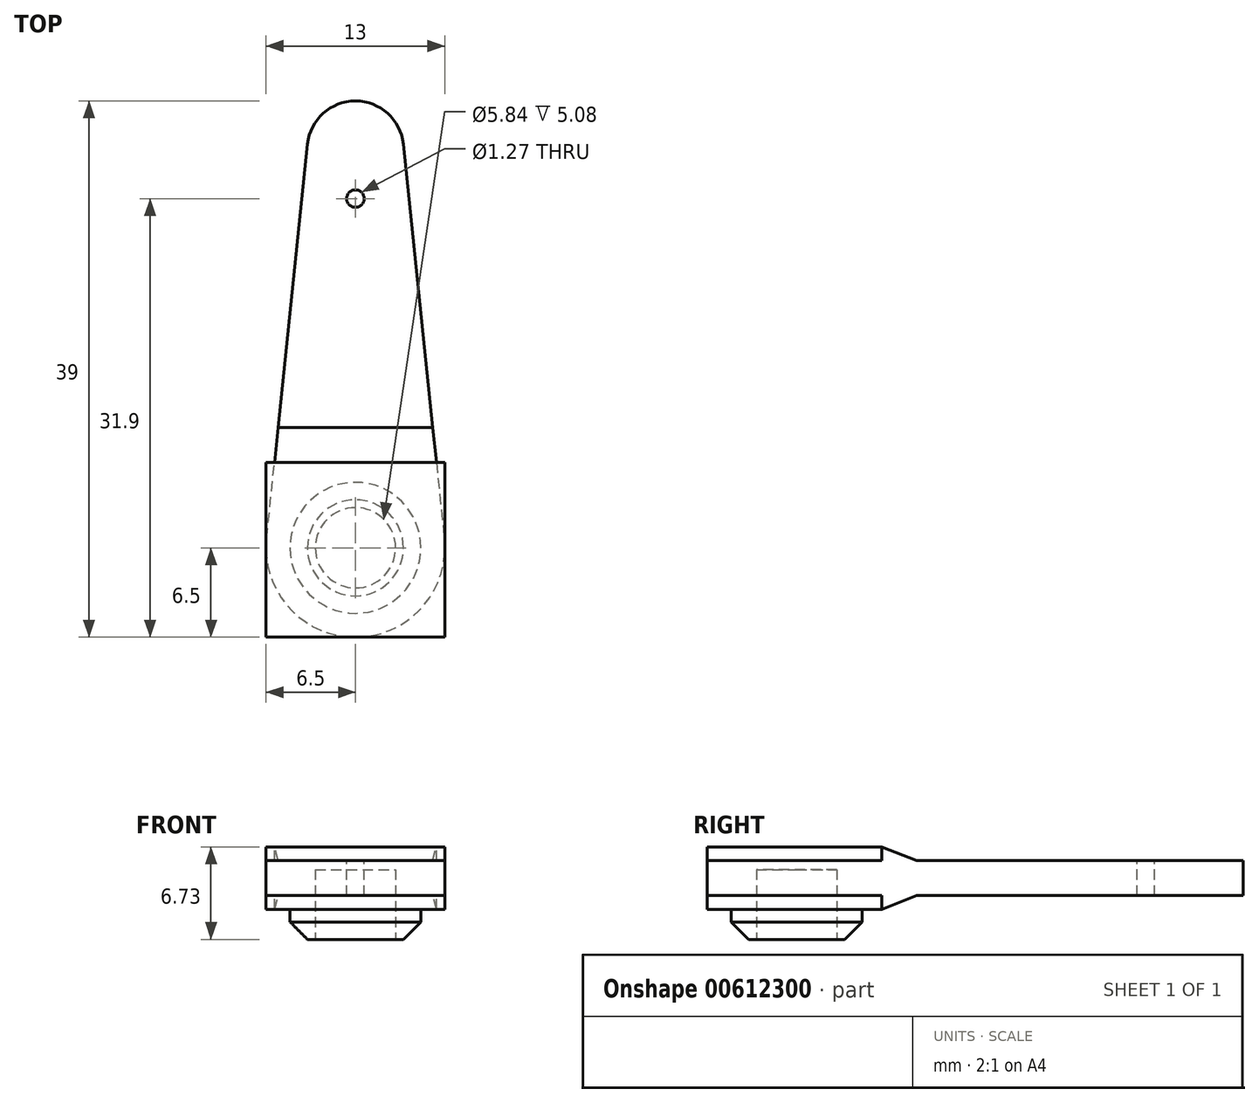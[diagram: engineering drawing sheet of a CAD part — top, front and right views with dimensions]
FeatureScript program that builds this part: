
annotation { "Feature Type Name" : "Feature", "Feature Type Description" : "" }
export const myFeature = defineFeature(function(context is Context, id is Id, definition is map)
    precondition{}
    {
        {
            var Q0;
            Q0=qCreatedBy(makeId("Top.planeOp"),FACE);
            var sketch = newSketch(context, id + "F0", { "sketchPlane" : qUnion([Q0])});
            skCircle(sketch, "E0", {"center": v(0, 0) * mm, "radius": 6.5 * mm});
            skCircle(sketch, "E1", {"center": v(0, 29) * mm, "radius": 3.5 * mm});
            skLineSegment(sketch, "E2", {"start": v(-6.47, 0.67) * mm, "end": v(-3.48, 29.36) * mm});
            skLineSegment(sketch, "E3", {"start": v(3.48, 29.36) * mm, "end": v(6.47, 0.67) * mm});
            skSolve(sketch);
        }
        {
            var Q0;
            Q0 = qSketchRegion(id + "F0", true);
            extrude(context, id + "F1", {"entities" : qUnion([Q0]), "endBound" : BoundingType.SYMMETRIC, "depth" : 2.54 * mm, "offsetDistance" : 25.4 * mm});
        }
        {
            var Q0;
            Q0=qCreatedBy(makeId("Right.planeOp"),FACE);
            var sketch = newSketch(context, id + "F2", { "sketchPlane" : qUnion([Q0])});
            skLineSegment(sketch, "E4.bottom", {"start": v(-6.5, 2.27) * mm, "end": v(6.2, 2.27) * mm});
            skLineSegment(sketch, "E4.top", {"start": v(-6.5, -2.27) * mm, "end": v(6.2, -2.27) * mm});
            skLineSegment(sketch, "E4.left", {"start": v(-6.5, 2.27) * mm, "end": v(-6.5, -2.27) * mm});
            skLineSegment(sketch, "E4.right", {"start": v(6.2, 2.27) * mm, "end": v(6.2, -2.27) * mm});
            skPoint(sketch, "E4.middle", {"position": v(-0.15, 0) * mm});
            skLineSegment(sketch, "E5.bottom", {"start": v(6.2, 1.27) * mm, "end": v(8.74, 1.27) * mm});
            skLineSegment(sketch, "E5.top", {"start": v(6.2, -1.27) * mm, "end": v(8.74, -1.27) * mm});
            skLineSegment(sketch, "E5.left", {"start": v(6.2, 1.27) * mm, "end": v(6.2, -1.27) * mm});
            skLineSegment(sketch, "E5.right", {"start": v(8.74, 1.27) * mm, "end": v(8.74, -1.27) * mm});
            skPoint(sketch, "E5.middle", {"position": v(7.47, 0) * mm});
            skLineSegment(sketch, "E6", {"start": v(6.2, 2.27) * mm, "end": v(8.74, 1.27) * mm});
            skLineSegment(sketch, "E7", {"start": v(8.74, -1.27) * mm, "end": v(6.2, -2.27) * mm});
            skLineSegment(sketch, "E8.bottom", {"start": v(6.2, 1.27) * mm, "end": v(-6.5, 1.27) * mm});
            skLineSegment(sketch, "E8.top", {"start": v(6.2, -1.27) * mm, "end": v(-6.5, -1.27) * mm});
            skLineSegment(sketch, "E8.right", {"start": v(-6.5, 1.27) * mm, "end": v(-6.5, -1.27) * mm});
            skSolve(sketch);
        }
        {
            var Q0;
            {var subQ0=sQuery(id+"F2.wireOp",EDGE,"E4.top");Q0=makeQuery(id+"F2.imprint","IMPRINT",FACE,{"disambiguationData":[TD([[makeQuery(id+"F2.imprint","IMPRINT",EDGE,{"derivedFrom":subQ0}),1.0]])]});}
            var Q1;
            {var subQ0=sQuery(id+"F2.wireOp",EDGE,"E4.bottom");Q1=makeQuery(id+"F2.imprint","IMPRINT",FACE,{"disambiguationData":[TD([[makeQuery(id+"F2.imprint","IMPRINT",EDGE,{"derivedFrom":subQ0}),-1.0]])]});}
            var Q2;
            {var subQ0=sQuery(id+"F2.wireOp",EDGE,"E6");Q2=makeQuery(id+"F2.imprint","IMPRINT",FACE,{"disambiguationData":[TD([[makeQuery(id+"F2.imprint","IMPRINT",EDGE,{"derivedFrom":subQ0}),-1.0]])]});}
            var Q3;
            {var subQ0=sQuery(id+"F2.wireOp",EDGE,"E7");Q3=makeQuery(id+"F2.imprint","IMPRINT",FACE,{"disambiguationData":[TD([[makeQuery(id+"F2.imprint","IMPRINT",EDGE,{"derivedFrom":subQ0}),-1.0]])]});}
            extrude(context, id + "F3", {"entities" : qUnion([Q0, Q1, Q2, Q3]), "operationType" : NewBodyOperationType.ADD, "endBound" : BoundingType.SYMMETRIC, "depth" : 13 * mm, "offsetDistance" : 25.4 * mm});
        }
        {
            var Q0;
            Q0=makeQuery(id+"F3.opExtrude","SWEPT_FACE",FACE,{"disambiguationData":[OSD([sQuery(id+"F2.wireOp",EDGE,"E4.bottom")])]});
            var sketch = newSketch(context, id + "F4", { "sketchPlane" : qUnion([Q0])});
            skArc(sketch, "E9.0.0", {"start": v(-6.47, 0.67) * mm, "mid": v(-6.5, 0.34) * mm, "end": v(-6.5, 0) * mm});
            skArc(sketch, "E9.0.1", {"start": v(-6.5, 0) * mm, "mid": v(-4.6, -4.6) * mm, "end": v(0, -6.5) * mm});
            skArc(sketch, "E9.0.2", {"start": v(0, -6.5) * mm, "mid": v(4.6, -4.6) * mm, "end": v(6.5, 0) * mm});
            skArc(sketch, "E9.0.3", {"start": v(6.5, 0) * mm, "mid": v(6.5, 0.34) * mm, "end": v(6.47, 0.67) * mm});
            skArc(sketch, "E9.0.5", {"start": v(6.47, 0.67) * mm, "mid": v(6.5, 0.34) * mm, "end": v(6.5, 0) * mm});
            skArc(sketch, "E9.0.6", {"start": v(6.5, 0) * mm, "mid": v(4.6, -4.6) * mm, "end": v(0, -6.5) * mm});
            skArc(sketch, "E9.0.7", {"start": v(0, -6.5) * mm, "mid": v(-4.6, -4.6) * mm, "end": v(-6.5, 0) * mm});
            skArc(sketch, "E9.0.8", {"start": v(-6.5, 0) * mm, "mid": v(-6.5, 0.34) * mm, "end": v(-6.47, 0.67) * mm});
            skLineSegment(sketch, "E10.0.0", {"start": v(5.63, 8.74) * mm, "end": v(3.48, 29.36) * mm});
            skLineSegment(sketch, "E10.0.2", {"start": v(3.48, 29.36) * mm, "end": v(5.63, 8.74) * mm});
            skLineSegment(sketch, "E10.0.3", {"start": v(5.63, 8.74) * mm, "end": v(6.47, 0.67) * mm});
            skLineSegment(sketch, "E10.0.5", {"start": v(6.47, 0.67) * mm, "end": v(5.63, 8.74) * mm});
            skLineSegment(sketch, "E11.0.0", {"start": v(-5.63, 8.74) * mm, "end": v(-6.47, 0.67) * mm});
            skLineSegment(sketch, "E11.0.2", {"start": v(-6.47, 0.67) * mm, "end": v(-5.63, 8.74) * mm});
            skLineSegment(sketch, "E11.0.3", {"start": v(-5.63, 8.74) * mm, "end": v(-3.48, 29.36) * mm});
            skLineSegment(sketch, "E11.0.5", {"start": v(-3.48, 29.36) * mm, "end": v(-5.63, 8.74) * mm});
            skLineSegment(sketch, "E12.0.0", {"start": v(-6.5, 6.2) * mm, "end": v(-6.5, -6.5) * mm});
            skLineSegment(sketch, "E12.0.1", {"start": v(-6.5, -6.5) * mm, "end": v(6.5, -6.5) * mm});
            skLineSegment(sketch, "E12.0.2", {"start": v(6.5, -6.5) * mm, "end": v(6.5, 6.2) * mm});
            skLineSegment(sketch, "E12.0.3", {"start": v(6.5, 6.2) * mm, "end": v(-6.5, 6.2) * mm});
            skLineSegment(sketch, "E13.0.0", {"start": v(-6.5, 8.74) * mm, "end": v(-6.5, 6.2) * mm});
            skLineSegment(sketch, "E13.0.1", {"start": v(-6.5, 6.2) * mm, "end": v(6.5, 6.2) * mm});
            skLineSegment(sketch, "E13.0.2", {"start": v(6.5, 6.2) * mm, "end": v(6.5, 8.74) * mm});
            skLineSegment(sketch, "E13.0.3", {"start": v(6.5, 8.74) * mm, "end": v(5.63, 8.74) * mm});
            skLineSegment(sketch, "E13.0.4", {"start": v(5.63, 8.74) * mm, "end": v(-5.63, 8.74) * mm});
            skLineSegment(sketch, "E13.0.5", {"start": v(-5.63, 8.74) * mm, "end": v(-6.5, 8.74) * mm});
            skSolve(sketch);
        }
        {
            var Q0;
            {var subQ4=sQuery(id+"F4.wireOp",EDGE,"E13.0.2");Q0=makeQuery(id+"F4.imprint","IMPRINT",FACE,{"disambiguationData":[TD([[makeQuery(id+"F4.imprint","IMPRINT",EDGE,{"derivedFrom":subQ4}),1.0]])]});}
            var Q1;
            {var subQ0=sQuery(id+"F4.wireOp",EDGE,"E9.0.5");Q1=makeQuery(id+"F4.imprint","IMPRINT",FACE,{"disambiguationData":[TD([[makeQuery(id+"F4.imprint","IMPRINT",EDGE,{"derivedFrom":subQ0}),1.0]])]});}
            var Q2;
            {var subQ0=sQuery(id+"F4.wireOp",EDGE,"E9.0.6");Q2=makeQuery(id+"F4.imprint","IMPRINT",FACE,{"disambiguationData":[TD([[makeQuery(id+"F4.imprint","IMPRINT",EDGE,{"derivedFrom":subQ0}),1.0]])]});}
            var Q3;
            {var subQ0=sQuery(id+"F4.wireOp",EDGE,"E9.0.7");Q3=makeQuery(id+"F4.imprint","IMPRINT",FACE,{"disambiguationData":[TD([[makeQuery(id+"F4.imprint","IMPRINT",EDGE,{"derivedFrom":subQ0}),1.0]])]});}
            var Q4;
            {var subQ4=sQuery(id+"F4.wireOp",EDGE,"E13.0.0");Q4=makeQuery(id+"F4.imprint","IMPRINT",FACE,{"disambiguationData":[TD([[makeQuery(id+"F4.imprint","IMPRINT",EDGE,{"derivedFrom":subQ4}),1.0]])]});}
            var Q5;
            {var subQ0=sQuery(id+"F4.wireOp",EDGE,"E9.0.8");Q5=makeQuery(id+"F4.imprint","IMPRINT",FACE,{"disambiguationData":[TD([[makeQuery(id+"F4.imprint","IMPRINT",EDGE,{"derivedFrom":subQ0}),1.0]])]});}
            extrude(context, id + "F5", {"entities" : qUnion([Q0, Q1, Q2, Q3, Q4, Q5]), "operationType" : NewBodyOperationType.REMOVE, "endBound" : BoundingType.THROUGH_ALL, "oppositeDirection" : true, "depth" : 25.4 * mm, "offsetDistance" : 25.4 * mm});
        }
        {
            var Q0;
            Q0=makeQuery(id+"F3.opExtrude","SWEPT_FACE",FACE,{"disambiguationData":[OSD([sQuery(id+"F2.wireOp",EDGE,"E4.top")])]});
            var sketch = newSketch(context, id + "F6", { "sketchPlane" : qUnion([Q0])});
            skCircle(sketch, "E14", {"center": v(0, 0) * mm, "radius": 4.76 * mm});
            skSolve(sketch);
        }
        {
            var Q0;
            Q0=makeQuery(id+"F6.imprint","IMPRINT",FACE,{"disambiguationData":[TD([[makeQuery(id+"F6.imprint","IMPRINT",EDGE,{"derivedFrom":sQuery(id+"F6.wireOp",EDGE,"E14")}),1.0]])]});
            extrude(context, id + "F7", {"entities" : qUnion([Q0]), "operationType" : NewBodyOperationType.ADD, "depth" : 2.18 * mm, "offsetDistance" : 25.4 * mm});
        }
        {
            var Q0;
            Q0=makeQuery(id+"F7.opExtrude","CAP_EDGE",EDGE,{"disambiguationData":[OSD([sQuery(id+"F6.wireOp",EDGE,"E14")])],"isStart":false});
            chamfer(context, id + "F8", {"entities" : qUnion([Q0]), "width" : 1.27 * mm, "tangentPropagation" : true});
        }
        {
            var Q0;
            Q0=makeQuery(id+"F7.opExtrude","CAP_FACE",FACE,{"disambiguationData":[OSD([sQuery(id+"F6.wireOp",EDGE,"E14")])],"isStart":false});
            var sketch = newSketch(context, id + "F9", { "sketchPlane" : qUnion([Q0])});
            skCircle(sketch, "E15", {"center": v(0, 0) * mm, "radius": 2.92 * mm});
            skSolve(sketch);
        }
        {
            var Q0;
            Q0 = qSketchRegion(id + "F9", true);
            extrude(context, id + "F10", {"entities" : qUnion([Q0]), "operationType" : NewBodyOperationType.REMOVE, "oppositeDirection" : true, "depth" : 5.08 * mm, "offsetDistance" : 25.4 * mm});
        }
        {
            var Q0;
            Q0=makeQuery(id+"F1.opExtrude","CAP_FACE",FACE,{"disambiguationData":[OSD([sQuery(id+"F0.wireOp",EDGE,"E0"),sQuery(id+"F0.wireOp",EDGE,"E1"),sQuery(id+"F0.wireOp",EDGE,"E2"),sQuery(id+"F0.wireOp",EDGE,"E3")])],"isStart":false});
            var sketch = newSketch(context, id + "F11", { "sketchPlane" : qUnion([Q0])});
            skCircle(sketch, "E16", {"center": v(0, 25.4) * mm, "radius": 0.64 * mm});
            skSolve(sketch);
        }
        {
            var Q0;
            Q0 = qSketchRegion(id + "F11", true);
            extrude(context, id + "F12", {"entities" : qUnion([Q0]), "operationType" : NewBodyOperationType.REMOVE, "oppositeDirection" : true, "depth" : 25.4 * mm, "offsetDistance" : 25.4 * mm});
        }
    });
